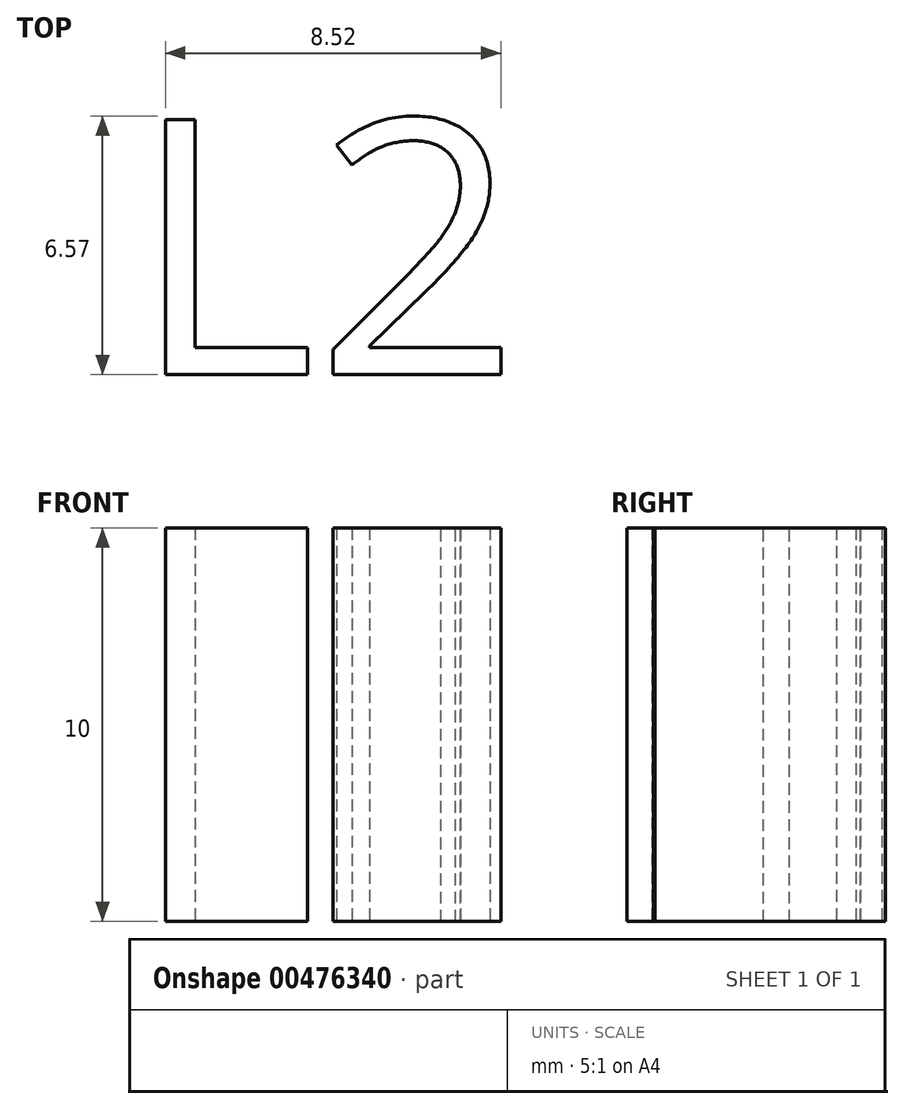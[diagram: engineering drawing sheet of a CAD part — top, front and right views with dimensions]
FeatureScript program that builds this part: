
annotation { "Feature Type Name" : "Feature", "Feature Type Description" : "" }
export const myFeature = defineFeature(function(context is Context, id is Id, definition is map)
    precondition{}
    {
        {
            var Q0;
            Q0=qCreatedBy(makeId("Top.planeOp"),FACE);
            var sketch = newSketch(context, id + "F0", { "sketchPlane" : qUnion([Q0])});
            skText(sketch, "E0", { "text": "L2\n", "fontName": "OpenSans-Regular.ttf"});
            skLineSegment(sketch, "E1", {"start": v(-5, 0) * mm, "end": v(5, 0) * mm, "construction": true});
            skLineSegment(sketch, "E2", {"start": v(0, 3.27) * mm, "end": v(0, -3.27) * mm, "construction": true});
            const initialGuessF0  = {"E0": [-0.005, -0.00327, 1, 0, 0.00653]};
            skSetInitialGuess(sketch, initialGuessF0);
            skSolve(sketch);
        }
        {
            var Q0;
            Q0 = qSketchRegion(id + "F0", true);
            extrude(context, id + "F1", {"entities" : qUnion([Q0]), "depth" : 10 * mm});
        }
    });
